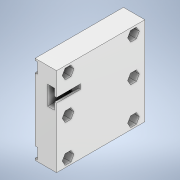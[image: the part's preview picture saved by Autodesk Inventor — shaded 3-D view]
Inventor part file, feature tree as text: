
AUTODESK INVENTOR PART (.ipt)
format: ipt  version: 2020 (Build 240168000, 168)  size: 221,184 bytes
history: native  units: mm
features: extrude x5, sketch x4, other x1, projected_geometry x1
ambient origin geometry x8: Origin, YZ Plane, XZ Plane, XY Plane, X Axis, Y Axis, Z Axis, Center Point
bodies: Body1 (feature_tree)
feature tree (11):
  other  "Bryła1"
  extrude  "Wyciągnięcie proste1"  Depth=74.0mm
  sketch  "Szkic2"
  extrude  "Wyciągnięcie proste2"  Depth=74.0mm
  extrude  "Wyciągnięcie proste3"  Depth=18.0mm TaperAngle=0.0deg
  extrude  "Wyciągnięcie proste4"  Depth=6.0mm
  extrude  "Wyciągnięcie proste5"  Depth=5.7mm
  sketch  "Szkic1"
  sketch  "Szkic3"
  sketch  "Szkic4"
  projected_geometry  "Pętla rzutowana1"
